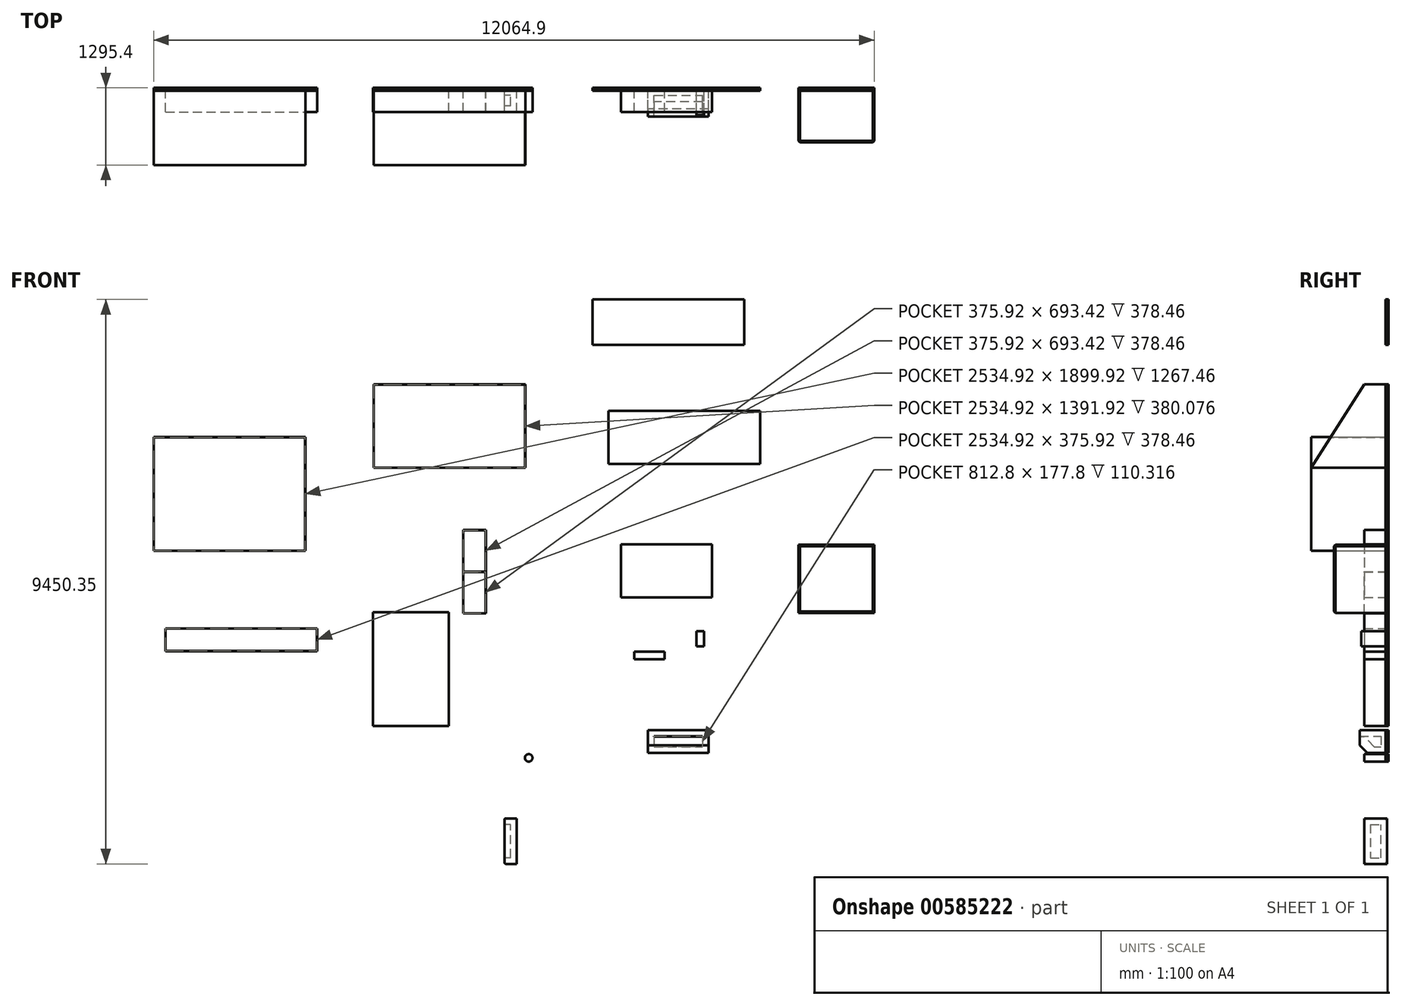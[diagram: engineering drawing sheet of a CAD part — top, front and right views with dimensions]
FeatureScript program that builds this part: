
annotation { "Feature Type Name" : "Feature", "Feature Type Description" : "" }
export const myFeature = defineFeature(function(context is Context, id is Id, definition is map)
    precondition{}
    {
        {
            var Q0;
            Q0=qCreatedBy(makeId("Front.planeOp"),FACE);
            var sketch = newSketch(context, id + "F0", { "sketchPlane" : qUnion([Q0])});
            skLineSegment(sketch, "E0.bottom", {"start": v(-190.5, 349.25) * mm, "end": v(190.5, 349.25) * mm});
            skLineSegment(sketch, "E0.top", {"start": v(-190.5, -349.25) * mm, "end": v(190.5, -349.25) * mm});
            skLineSegment(sketch, "E0.left", {"start": v(-190.5, 349.25) * mm, "end": v(-190.5, -349.25) * mm});
            skLineSegment(sketch, "E0.right", {"start": v(190.5, 349.25) * mm, "end": v(190.5, -349.25) * mm});
            skPoint(sketch, "E0.middle", {"position": v(0, 0) * mm});
            skLineSegment(sketch, "E1.bottom", {"start": v(-5372.21, 1905) * mm, "end": v(-2832.21, 1905) * mm});
            skLineSegment(sketch, "E1.top", {"start": v(-5372.21, 0) * mm, "end": v(-2832.21, 0) * mm});
            skLineSegment(sketch, "E1.left", {"start": v(-5372.21, 1905) * mm, "end": v(-5372.21, 0) * mm});
            skLineSegment(sketch, "E1.right", {"start": v(-2832.21, 1905) * mm, "end": v(-2832.21, 0) * mm});
            skLineSegment(sketch, "E2.bottom", {"start": v(-1688.53, 2789.3) * mm, "end": v(851.47, 2789.3) * mm});
            skLineSegment(sketch, "E2.top", {"start": v(-1688.53, 1392.3) * mm, "end": v(851.47, 1392.3) * mm});
            skLineSegment(sketch, "E2.left", {"start": v(-1688.53, 2789.3) * mm, "end": v(-1688.53, 1392.3) * mm});
            skLineSegment(sketch, "E2.right", {"start": v(851.47, 2789.3) * mm, "end": v(851.47, 1392.3) * mm});
            skLineSegment(sketch, "E3.bottom", {"start": v(-5175.06, -1297.6) * mm, "end": v(-2635.06, -1297.6) * mm});
            skLineSegment(sketch, "E3.top", {"start": v(-5175.06, -1678.6) * mm, "end": v(-2635.06, -1678.6) * mm});
            skLineSegment(sketch, "E3.left", {"start": v(-5175.06, -1297.6) * mm, "end": v(-5175.06, -1678.6) * mm});
            skLineSegment(sketch, "E3.right", {"start": v(-2635.06, -1297.6) * mm, "end": v(-2635.06, -1678.6) * mm});
            skLineSegment(sketch, "E4.bottom", {"start": v(2245.93, 2345.16) * mm, "end": v(4785.93, 2345.16) * mm});
            skLineSegment(sketch, "E4.top", {"start": v(2245.93, 1456.16) * mm, "end": v(4785.93, 1456.16) * mm});
            skLineSegment(sketch, "E4.left", {"start": v(2245.93, 2345.16) * mm, "end": v(2245.93, 1456.16) * mm});
            skLineSegment(sketch, "E4.right", {"start": v(4785.93, 2345.16) * mm, "end": v(4785.93, 1456.16) * mm});
            skLineSegment(sketch, "E5.bottom", {"start": v(2455.76, 109.88) * mm, "end": v(3979.76, 109.88) * mm});
            skLineSegment(sketch, "E5.top", {"start": v(2455.76, -779.12) * mm, "end": v(3979.76, -779.12) * mm});
            skLineSegment(sketch, "E5.left", {"start": v(2455.76, 109.88) * mm, "end": v(2455.76, -779.12) * mm});
            skLineSegment(sketch, "E5.right", {"start": v(3979.76, 109.88) * mm, "end": v(3979.76, -779.12) * mm});
            skLineSegment(sketch, "E6.bottom", {"start": v(2678.23, -1683.89) * mm, "end": v(3186.23, -1683.89) * mm});
            skLineSegment(sketch, "E6.top", {"start": v(2678.23, -1810.89) * mm, "end": v(3186.23, -1810.89) * mm});
            skLineSegment(sketch, "E6.left", {"start": v(2678.23, -1683.89) * mm, "end": v(2678.23, -1810.89) * mm});
            skLineSegment(sketch, "E6.right", {"start": v(3186.23, -1683.89) * mm, "end": v(3186.23, -1810.89) * mm});
            skLineSegment(sketch, "E7.bottom", {"start": v(3716.56, -1343.12) * mm, "end": v(3843.56, -1343.12) * mm});
            skLineSegment(sketch, "E7.top", {"start": v(3716.56, -1597.12) * mm, "end": v(3843.56, -1597.12) * mm});
            skLineSegment(sketch, "E7.left", {"start": v(3716.56, -1343.12) * mm, "end": v(3716.56, -1597.12) * mm});
            skLineSegment(sketch, "E7.right", {"start": v(3843.56, -1343.12) * mm, "end": v(3843.56, -1597.12) * mm});
            skLineSegment(sketch, "E8.bottom", {"start": v(-1697.55, -1027.44) * mm, "end": v(-427.55, -1027.44) * mm});
            skLineSegment(sketch, "E8.top", {"start": v(-1697.55, -2932.44) * mm, "end": v(-427.55, -2932.44) * mm});
            skLineSegment(sketch, "E8.left", {"start": v(-1697.55, -1027.44) * mm, "end": v(-1697.55, -2932.44) * mm});
            skLineSegment(sketch, "E8.right", {"start": v(-427.55, -1027.44) * mm, "end": v(-427.55, -2932.44) * mm});
            skLineSegment(sketch, "E9.bottom", {"start": v(5422.72, 101.75) * mm, "end": v(6692.72, 101.75) * mm});
            skLineSegment(sketch, "E9.top", {"start": v(5422.72, -1041.25) * mm, "end": v(6692.72, -1041.25) * mm});
            skLineSegment(sketch, "E9.left", {"start": v(5422.72, 101.75) * mm, "end": v(5422.72, -1041.25) * mm});
            skLineSegment(sketch, "E9.right", {"start": v(6692.72, 101.75) * mm, "end": v(6692.72, -1041.25) * mm});
            skLineSegment(sketch, "E10.bottom", {"start": v(1974.36, 4210.52) * mm, "end": v(4514.36, 4210.52) * mm});
            skLineSegment(sketch, "E10.top", {"start": v(1974.36, 3448.52) * mm, "end": v(4514.36, 3448.52) * mm});
            skLineSegment(sketch, "E10.left", {"start": v(1974.36, 4210.52) * mm, "end": v(1974.36, 3448.52) * mm});
            skLineSegment(sketch, "E10.right", {"start": v(4514.36, 4210.52) * mm, "end": v(4514.36, 3448.52) * mm});
            skLineSegment(sketch, "E11.bottom", {"start": v(349.2, -3715.83) * mm, "end": v(552.4, -3715.83) * mm});
            skLineSegment(sketch, "E11.top", {"start": v(349.2, -4477.83) * mm, "end": v(552.4, -4477.83) * mm});
            skLineSegment(sketch, "E11.left", {"start": v(349.2, -3715.83) * mm, "end": v(349.2, -4477.83) * mm});
            skLineSegment(sketch, "E11.right", {"start": v(552.4, -3715.83) * mm, "end": v(552.4, -4477.83) * mm});
            skCircle(sketch, "E12", {"center": v(908.16, -3464.75) * mm, "radius": 63.5 * mm});
            skLineSegment(sketch, "E13.bottom", {"start": v(2906.58, -2999.99) * mm, "end": v(3922.58, -2999.99) * mm});
            skLineSegment(sketch, "E13.top", {"start": v(2906.58, -3380.99) * mm, "end": v(3922.58, -3380.99) * mm});
            skLineSegment(sketch, "E13.left", {"start": v(2906.58, -2999.99) * mm, "end": v(2906.58, -3380.99) * mm});
            skLineSegment(sketch, "E13.right", {"start": v(3922.58, -2999.99) * mm, "end": v(3922.58, -3380.99) * mm});
            skSolve(sketch);
        }
        {
            var Q0;
            Q0 = qSketchRegion(id + "F0", true);
            extrude(context, id + "F1", {"entities" : qUnion([Q0]), "depth" : 381 * mm, "offsetDistance" : 25.4 * mm});
        }
        {
            var Q0;
            Q0=makeQuery(id+"F1.opExtrude","CAP_FACE",FACE,{"disambiguationData":[OSD([sQuery(id+"F0.wireOp",EDGE,"E0.bottom"),sQuery(id+"F0.wireOp",EDGE,"E0.top"),sQuery(id+"F0.wireOp",EDGE,"E0.left"),sQuery(id+"F0.wireOp",EDGE,"E0.right")])],"isStart":false});
            shell(context, id + "F2", {"entities" : qUnion([Q0]), "thickness" : 2.54 * mm});
        }
        {
            var Q0;
            Q0=makeQuery(id+"F1.opExtrude","SWEPT_BODY",BODY,{"disambiguationData":[OSD([sQuery(id+"F0.wireOp",EDGE,"E0.bottom"),sQuery(id+"F0.wireOp",EDGE,"E0.top"),sQuery(id+"F0.wireOp",EDGE,"E0.left"),sQuery(id+"F0.wireOp",EDGE,"E0.right")])]});
            var Q1;
            Q1=makeQuery(id+"F1.opExtrude","SWEPT_FACE",FACE,{"disambiguationData":[OSD([sQuery(id+"F0.wireOp",EDGE,"E0.top")])]});
            mirror(context, id + "F3", {"operationType" : NewBodyOperationType.ADD, "entities" : qUnion([Q0]), "mirrorPlane" : qUnion([Q1])});
        }
        {
            var Q0;
            Q0=makeQuery(id+"F1.opExtrude","CAP_FACE",FACE,{"disambiguationData":[OSD([sQuery(id+"F0.wireOp",EDGE,"E1.bottom"),sQuery(id+"F0.wireOp",EDGE,"E1.top"),sQuery(id+"F0.wireOp",EDGE,"E1.left"),sQuery(id+"F0.wireOp",EDGE,"E1.right")])],"isStart":false});
            extrude(context, id + "F4", {"entities" : qUnion([Q0]), "operationType" : NewBodyOperationType.ADD, "depth" : 889 * mm, "offsetDistance" : 25.4 * mm});
        }
        {
            var Q0;
            Q0=makeQuery(id+"F4.opExtrude","CAP_FACE",FACE,{"disambiguationData":[OSD([sQuery(id+"F0.wireOp",EDGE,"E1.bottom"),sQuery(id+"F0.wireOp",EDGE,"E1.top"),sQuery(id+"F0.wireOp",EDGE,"E1.left"),sQuery(id+"F0.wireOp",EDGE,"E1.right")])],"isStart":false});
            shell(context, id + "F5", {"entities" : qUnion([Q0]), "thickness" : 2.54 * mm});
        }
        {
            var Q0;
            Q0=makeQuery(id+"F1.opExtrude","CAP_FACE",FACE,{"disambiguationData":[OSD([sQuery(id+"F0.wireOp",EDGE,"E2.bottom"),sQuery(id+"F0.wireOp",EDGE,"E2.top"),sQuery(id+"F0.wireOp",EDGE,"E2.left"),sQuery(id+"F0.wireOp",EDGE,"E2.right")])],"isStart":false});
            extrude(context, id + "F6", {"entities" : qUnion([Q0]), "operationType" : NewBodyOperationType.ADD, "depth" : 889 * mm, "offsetDistance" : 25.4 * mm});
        }
        {
            var Q0;
            Q0=makeQuery(id+"F6.opExtrude","CAP_EDGE",EDGE,{"disambiguationData":[OSD([sQuery(id+"F0.wireOp",EDGE,"E2.bottom")])],"isStart":false});
            chamfer(context, id + "F7", {"entities" : qUnion([Q0]), "chamferType" : ChamferType.TWO_OFFSETS, "width1" : 889 * mm, "oppositeDirection" : false, "width2" : 1397 * mm});
        }
        {
            var Q0;
            Q0=makeQuery(id+"F7.opChamfer","BLEND_FACE",FACE,{"disambiguationData":[OSD([sQuery(id+"F0.wireOp",EDGE,"E2.bottom")])]});
            shell(context, id + "F8", {"entities" : qUnion([Q0]), "thickness" : 2.54 * mm});
        }
        {
            var Q0;
            Q0 = qSketchRegion(id + "F0", true);
            extrude(context, id + "F9", {"entities" : qUnion([Q0]), "depth" : 25.4 * mm, "offsetDistance" : 25.4 * mm});
        }
        {
            var Q0;
            Q0=makeQuery(id+"F1.opExtrude","CAP_FACE",FACE,{"disambiguationData":[OSD([sQuery(id+"F0.wireOp",EDGE,"E3.bottom"),sQuery(id+"F0.wireOp",EDGE,"E3.top"),sQuery(id+"F0.wireOp",EDGE,"E3.left"),sQuery(id+"F0.wireOp",EDGE,"E3.right")])],"isStart":false});
            shell(context, id + "F10", {"entities" : qUnion([Q0]), "thickness" : 2.54 * mm});
        }
        {
            var Q0;
            Q0=makeQuery(id+"F1.opExtrude","CAP_FACE",FACE,{"disambiguationData":[OSD([sQuery(id+"F0.wireOp",EDGE,"E7.bottom"),sQuery(id+"F0.wireOp",EDGE,"E7.top"),sQuery(id+"F0.wireOp",EDGE,"E7.left"),sQuery(id+"F0.wireOp",EDGE,"E7.right")])],"isStart":false});
            extrude(context, id + "F11", {"entities" : qUnion([Q0]), "operationType" : NewBodyOperationType.ADD, "depth" : 50.8 * mm, "offsetDistance" : 25.4 * mm});
        }
        {
            var Q0;
            Q0=makeQuery(id+"F1.opExtrude","CAP_FACE",FACE,{"disambiguationData":[OSD([sQuery(id+"F0.wireOp",EDGE,"E9.bottom"),sQuery(id+"F0.wireOp",EDGE,"E9.top"),sQuery(id+"F0.wireOp",EDGE,"E9.left"),sQuery(id+"F0.wireOp",EDGE,"E9.right")])],"isStart":false});
            extrude(context, id + "F12", {"entities" : qUnion([Q0]), "operationType" : NewBodyOperationType.ADD, "depth" : 508 * mm, "offsetDistance" : 25.4 * mm});
        }
        {
            var Q0;
            Q0=makeQuery(id+"F12.opExtrude","CAP_FACE",FACE,{"disambiguationData":[OSD([sQuery(id+"F0.wireOp",EDGE,"E9.bottom"),sQuery(id+"F0.wireOp",EDGE,"E9.top"),sQuery(id+"F0.wireOp",EDGE,"E9.left"),sQuery(id+"F0.wireOp",EDGE,"E9.right")])],"isStart":false});
            var Q1;
            {var subQ0=sQuery(id+"F0.wireOp",EDGE,"E9.bottom");Q1=makeQuery(id+"F12.boolean.opBoolean","MERGE",FACE,{"derivedFrom":[makeQuery(id+"F1.opExtrude","SWEPT_FACE",FACE,{"disambiguationData":[OSD([subQ0])]}),makeQuery(id+"F12.opExtrude","SWEPT_FACE",FACE,{"disambiguationData":[OSD([subQ0])]})]});}
            chamfer(context, id + "F13", {"entities" : qUnion([Q0, Q1]), "width" : 25.4 * mm});
        }
        {
            var Q0;
            Q0 = qSketchRegion(id + "F0", true);
            extrude(context, id + "F14", {"entities" : qUnion([Q0]), "oppositeDirection" : true, "depth" : 25.4 * mm, "offsetDistance" : 25.4 * mm});
        }
        {
            var Q0;
            Q0=makeQuery(id+"F1.opExtrude","SWEPT_BODY",BODY,{"disambiguationData":[OSD([sQuery(id+"F0.wireOp",EDGE,"E4.bottom"),sQuery(id+"F0.wireOp",EDGE,"E4.top"),sQuery(id+"F0.wireOp",EDGE,"E4.left"),sQuery(id+"F0.wireOp",EDGE,"E4.right")])]});
            deleteBodies(context, id + "F15", {"entities" : qUnion([Q0])});
        }
        {
            var Q0;
            Q0=makeQuery(id+"F1.opExtrude","SWEPT_BODY",BODY,{"disambiguationData":[OSD([sQuery(id+"F0.wireOp",EDGE,"E10.bottom"),sQuery(id+"F0.wireOp",EDGE,"E10.top"),sQuery(id+"F0.wireOp",EDGE,"E10.left"),sQuery(id+"F0.wireOp",EDGE,"E10.right")])]});
            deleteBodies(context, id + "F16", {"entities" : qUnion([Q0])});
        }
        {
            var Q0;
            Q0=makeQuery(id+"F1.opExtrude","SWEPT_FACE",FACE,{"disambiguationData":[OSD([sQuery(id+"F0.wireOp",EDGE,"E11.right")])]});
            var Q1;
            Q1=makeQuery(id+"F9.opExtrude","CAP_EDGE",EDGE,{"disambiguationData":[OSD([sQuery(id+"F0.wireOp",EDGE,"E11.right")])],"isStart":false});
            fillet(context, id + "F17", {"entities" : qUnion([Q0, Q1]), "radius" : 25.4 * mm, "tangentPropagation" : true, "allowEdgeOverflow" : false});
        }
        {
            var Q0;
            Q0=makeQuery(id+"F1.opExtrude","SWEPT_FACE",FACE,{"disambiguationData":[OSD([sQuery(id+"F0.wireOp",EDGE,"E11.right")])]});
            shell(context, id + "F18", {"entities" : qUnion([Q0]), "thickness" : 101.6 * mm});
        }
        {
            var Q0;
            Q0=makeQuery(id+"F1.opExtrude","SWEPT_BODY",BODY,{"disambiguationData":[OSD([sQuery(id+"F0.wireOp",EDGE,"E11.bottom"),sQuery(id+"F0.wireOp",EDGE,"E11.top"),sQuery(id+"F0.wireOp",EDGE,"E11.left"),sQuery(id+"F0.wireOp",EDGE,"E11.right")])]});
            var Q1;
            {var subQ0=sQuery(id+"F0.wireOp",EDGE,"E11.top");Q1=makeQuery(id+"F17.opFillet","BLEND_EDGE",EDGE,{"blendedFrom":[makeQuery(id+"F1.opExtrude","SWEPT_EDGE",EDGE,{"disambiguationData":[OSD([subQ0,sQuery(id+"F0.wireOp",EDGE,"E11.right")])]}),makeQuery(id+"F1.opExtrude","SWEPT_FACE",FACE,{"disambiguationData":[OSD([subQ0])]})],"blendedInto":[makeQuery(id+"F1.opExtrude","SWEPT_FACE",FACE,{"disambiguationData":[OSD([subQ0])]})]});}
            transform(context, id + "F19", {"entities" : qUnion([Q0]), "transformType" : TransformType.ROTATION, "transformAxis" : qUnion([Q1]), "angle" : 180 * degree, "makeCopy" : false});
        }
        {
            var Q0;
            Q0=makeQuery(id+"F9.opExtrude","SWEPT_BODY",BODY,{"disambiguationData":[OSD([sQuery(id+"F0.wireOp",EDGE,"E11.bottom"),sQuery(id+"F0.wireOp",EDGE,"E11.top"),sQuery(id+"F0.wireOp",EDGE,"E11.left"),sQuery(id+"F0.wireOp",EDGE,"E11.right")])]});
            deleteBodies(context, id + "F20", {"entities" : qUnion([Q0])});
        }
        {
            var Q0;
            Q0=makeQuery(id+"F14.opExtrude","SWEPT_BODY",BODY,{"disambiguationData":[OSD([sQuery(id+"F0.wireOp",EDGE,"E11.bottom"),sQuery(id+"F0.wireOp",EDGE,"E11.top"),sQuery(id+"F0.wireOp",EDGE,"E11.left"),sQuery(id+"F0.wireOp",EDGE,"E11.right")])]});
            deleteBodies(context, id + "F21", {"entities" : qUnion([Q0])});
        }
        {
            var Q0;
            Q0=makeQuery(id+"F1.opExtrude","CAP_EDGE",EDGE,{"disambiguationData":[OSD([sQuery(id+"F0.wireOp",EDGE,"E13.top")])],"isStart":false});
            chamfer(context, id + "F22", {"entities" : qUnion([Q0]), "width" : 127 * mm, "tangentPropagation" : true});
        }
        {
            var Q0;
            Q0=makeQuery(id+"F1.opExtrude","CAP_FACE",FACE,{"disambiguationData":[OSD([sQuery(id+"F0.wireOp",EDGE,"E13.bottom"),sQuery(id+"F0.wireOp",EDGE,"E13.top"),sQuery(id+"F0.wireOp",EDGE,"E13.left"),sQuery(id+"F0.wireOp",EDGE,"E13.right")])],"isStart":false});
            shell(context, id + "F23", {"entities" : qUnion([Q0]), "thickness" : 101.6 * mm});
        }
        {
            var Q0;
            Q0=makeQuery(id+"F1.opExtrude","CAP_FACE",FACE,{"disambiguationData":[OSD([sQuery(id+"F0.wireOp",EDGE,"E13.bottom"),sQuery(id+"F0.wireOp",EDGE,"E13.top"),sQuery(id+"F0.wireOp",EDGE,"E13.left"),sQuery(id+"F0.wireOp",EDGE,"E13.right")])],"isStart":false});
            var Q1;
            Q1=makeQuery(id+"F22.opChamfer","BLEND_FACE",FACE,{"disambiguationData":[OSD([sQuery(id+"F0.wireOp",EDGE,"E13.top")])]});
            extrude(context, id + "F24", {"entities" : qUnion([Q0, Q1]), "operationType" : NewBodyOperationType.ADD, "depth" : 76.2 * mm, "offsetDistance" : 25.4 * mm});
        }
    });
